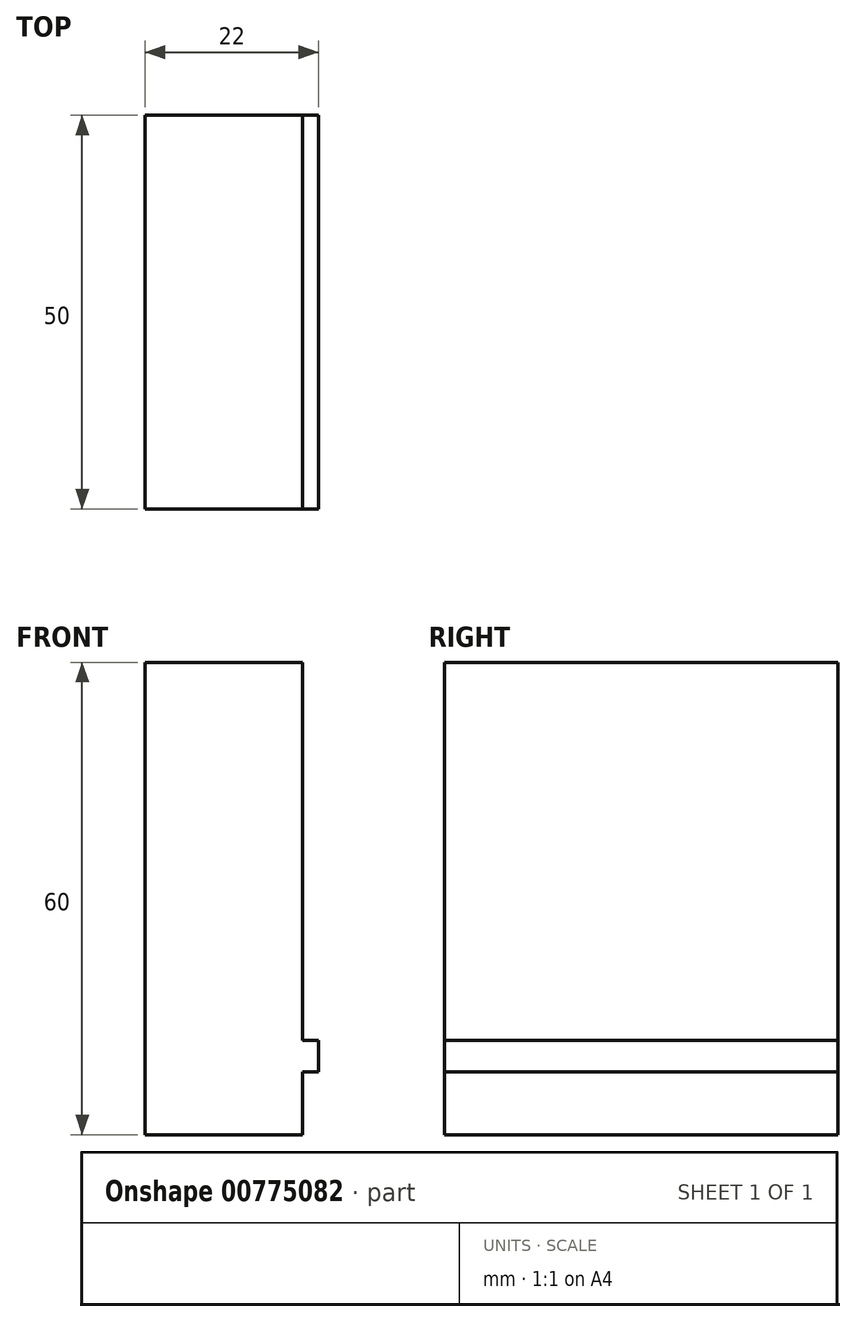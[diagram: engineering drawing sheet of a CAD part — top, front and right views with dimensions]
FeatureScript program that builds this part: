
annotation { "Feature Type Name" : "Feature", "Feature Type Description" : "" }
export const myFeature = defineFeature(function(context is Context, id is Id, definition is map)
    precondition{}
    {
        {
            var Q0;
            Q0=qCreatedBy(makeId("Top.planeOp"),FACE);
            var sketch = newSketch(context, id + "F0", { "sketchPlane" : qUnion([Q0])});
            skLineSegment(sketch, "E0.bottom", {"start": v(-10, 25) * mm, "end": v(10, 25) * mm});
            skLineSegment(sketch, "E0.top", {"start": v(-10, -25) * mm, "end": v(10, -25) * mm});
            skLineSegment(sketch, "E0.left", {"start": v(-10, 25) * mm, "end": v(-10, -25) * mm});
            skLineSegment(sketch, "E0.right", {"start": v(10, 25) * mm, "end": v(10, -25) * mm});
            skSolve(sketch);
        }
        {
            var Q0;
            Q0 = qSketchRegion(id + "F0", true);
            extrude(context, id + "F1", {"entities" : qUnion([Q0]), "depth" : 60 * mm, "offsetDistance" : 25 * mm});
        }
        {
            var Q0;
            Q0=makeQuery(id+"F1.opExtrude","SWEPT_FACE",FACE,{"disambiguationData":[OSD([sQuery(id+"F0.wireOp",EDGE,"E0.right")])]});
            var sketch = newSketch(context, id + "F2", { "sketchPlane" : qUnion([Q0])});
            skCircle(sketch, "E1", {"center": v(-14.78, 10) * mm, "radius": 2.5 * mm});
            skCircle(sketch, "E2", {"center": v(1.15, 10) * mm, "radius": 2.5 * mm});
            skSolve(sketch);
        }
        {
            var Q0;
            Q0=makeQuery(id+"F2.imprint","IMPRINT",FACE,{"disambiguationData":[TD([[makeQuery(id+"F2.imprint","IMPRINT",EDGE,{"derivedFrom":sQuery(id+"F2.wireOp",EDGE,"E1")}),-1.0]])]});
            var sketch = newSketch(context, id + "F3", { "sketchPlane" : qUnion([Q0])});
            skLineSegment(sketch, "E3.bottom", {"start": v(-25, 12) * mm, "end": v(25, 12) * mm});
            skLineSegment(sketch, "E3.top", {"start": v(-25, 8) * mm, "end": v(25, 8) * mm});
            skLineSegment(sketch, "E3.left", {"start": v(-25, 12) * mm, "end": v(-25, 8) * mm});
            skLineSegment(sketch, "E3.right", {"start": v(25, 12) * mm, "end": v(25, 8) * mm});
            skSolve(sketch);
        }
        {
            var Q0;
            Q0 = qSketchRegion(id + "F3", true);
            extrude(context, id + "F4", {"entities" : qUnion([Q0]), "operationType" : NewBodyOperationType.ADD, "depth" : 2 * mm, "offsetDistance" : 25 * mm});
        }
    });
